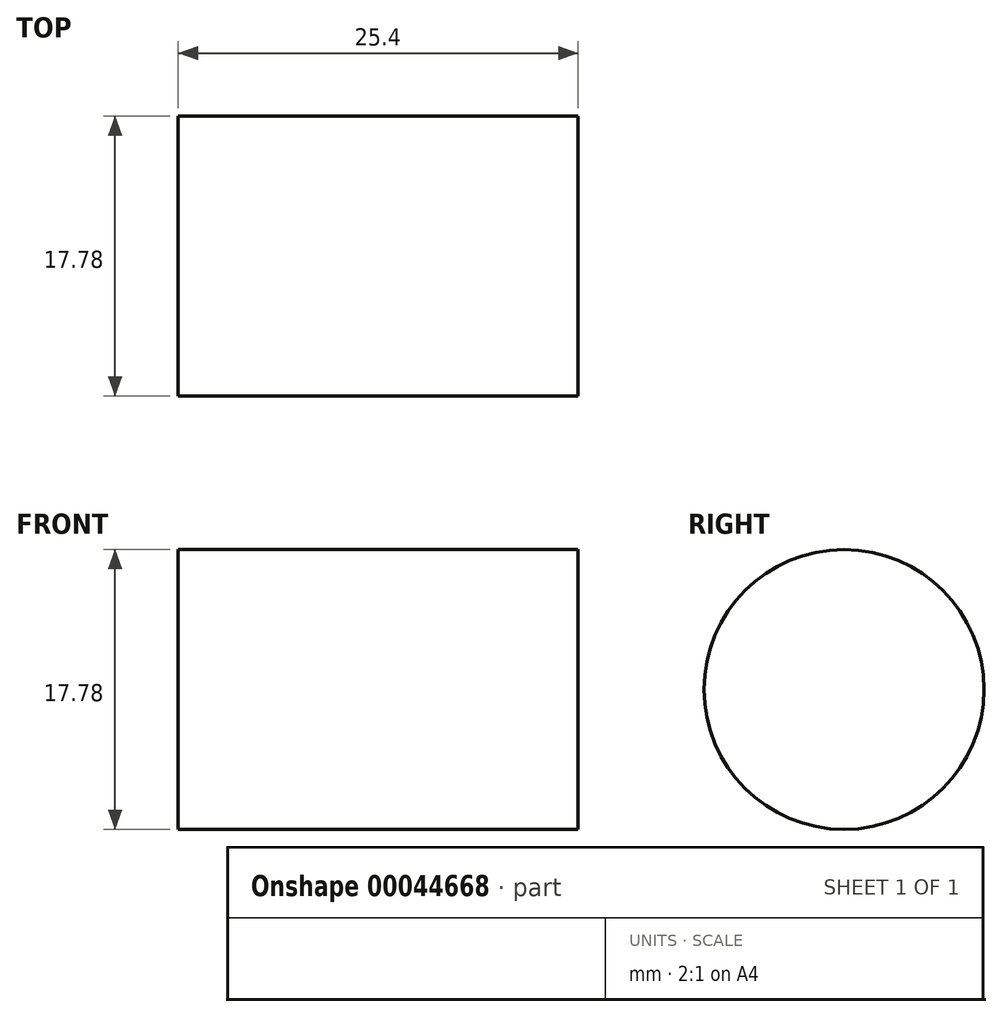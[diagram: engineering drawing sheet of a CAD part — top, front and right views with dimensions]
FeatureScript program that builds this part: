
annotation { "Feature Type Name" : "Feature", "Feature Type Description" : "" }
export const myFeature = defineFeature(function(context is Context, id is Id, definition is map)
    precondition{}
    {
        {
            var Q0;
            Q0=qCreatedBy(makeId("Right.planeOp"),FACE);
            var sketch = newSketch(context, id + "F0", { "sketchPlane" : qUnion([Q0])});
            skCircle(sketch, "E0", {"center": v(0, 0) * mm, "radius": 8.9 * mm});
            skSolve(sketch);
        }
        {
            var Q0;
            Q0=makeQuery(id+"F0.imprint","IMPRINT",FACE,{"disambiguationData":[TD([[makeQuery(id+"F0.imprint","IMPRINT",EDGE,{"derivedFrom":sQuery(id+"F0.wireOp",EDGE,"E0")}),1.0]])]});
            extrude(context, id + "F1", {"entities" : qUnion([Q0]), "depth" : 25.4 * mm});
        }
    });
